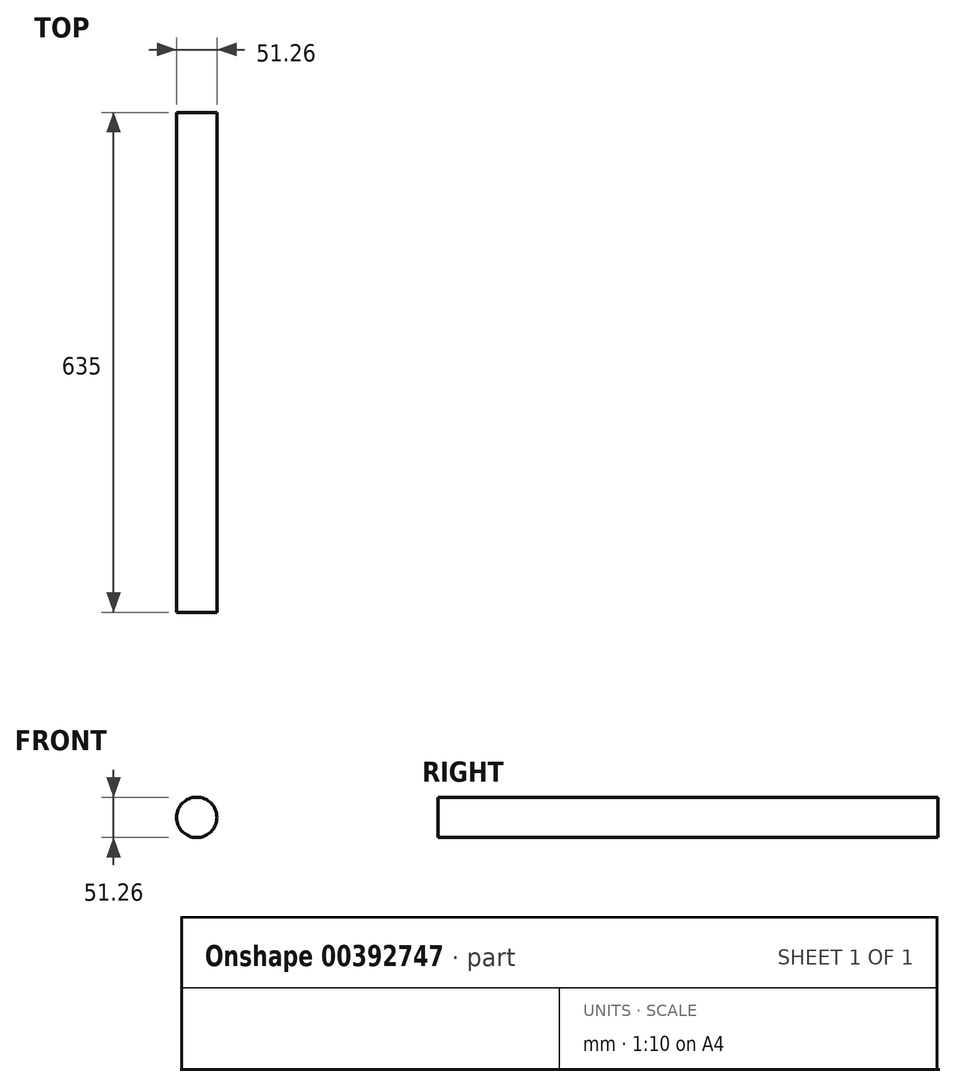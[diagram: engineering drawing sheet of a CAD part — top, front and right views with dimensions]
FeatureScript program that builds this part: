
annotation { "Feature Type Name" : "Feature", "Feature Type Description" : "" }
export const myFeature = defineFeature(function(context is Context, id is Id, definition is map)
    precondition{}
    {
        {
            var Q0;
            Q0=qCreatedBy(makeId("Front.planeOp"),FACE);
            var sketch = newSketch(context, id + "F0", { "sketchPlane" : qUnion([Q0])});
            skCircle(sketch, "E0", {"center": v(0, 0) * mm, "radius": 25.63 * mm});
            skSolve(sketch);
        }
        {
            var Q0;
            Q0 = qSketchRegion(id + "F0", true);
            extrude(context, id + "F1", {"entities" : qUnion([Q0]), "depth" : 635 * mm});
        }
    });
